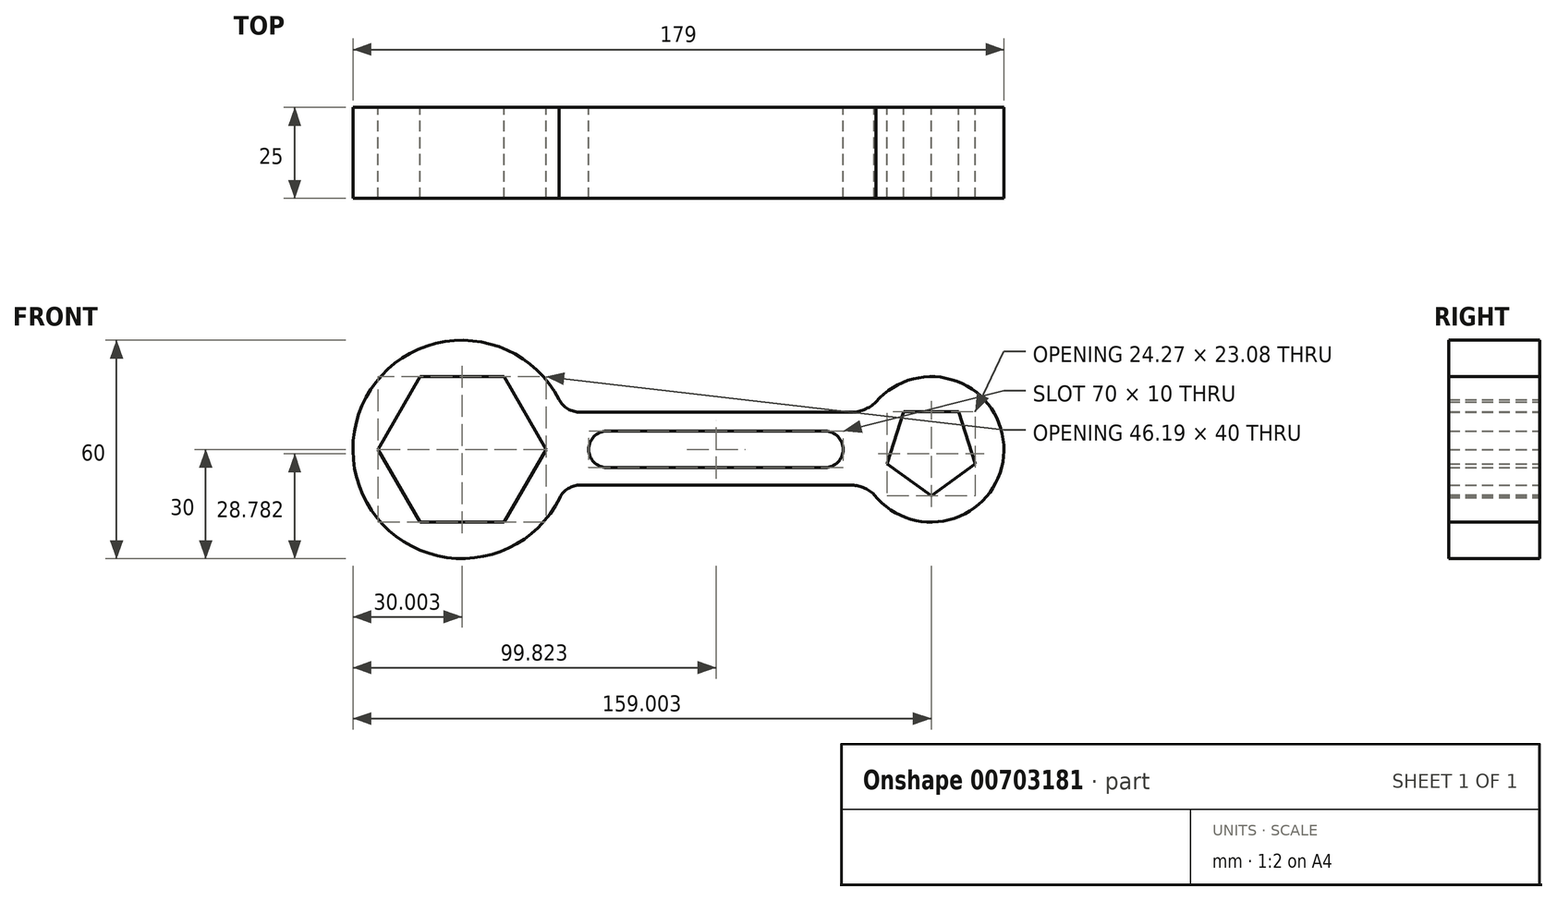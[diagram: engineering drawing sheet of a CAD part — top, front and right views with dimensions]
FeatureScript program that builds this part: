
annotation { "Feature Type Name" : "Feature", "Feature Type Description" : "" }
export const myFeature = defineFeature(function(context is Context, id is Id, definition is map)
    precondition{}
    {
        {
            var Q0;
            Q0=qCreatedBy(makeId("Front.planeOp"),FACE);
            var sketch = newSketch(context, id + "F0", { "sketchPlane" : qUnion([Q0])});
            skArc(sketch, "E0", {"start": v(7.25, 5) * mm, "mid": v(2.25, 0) * mm, "end": v(7.25, -5) * mm});
            skArc(sketch, "E1", {"start": v(67.25, -5) * mm, "mid": v(72.25, 0) * mm, "end": v(67.25, 5) * mm});
            skLineSegment(sketch, "E2", {"start": v(7.25, 5) * mm, "end": v(67.25, 5) * mm});
            skLineSegment(sketch, "E3", {"start": v(7.25, -5) * mm, "end": v(67.25, -5) * mm});
            skCircle(sketch, "E4", {"center": v(-32.57, 0) * mm, "radius": 30 * mm});
            skCircle(sketch, "E5", {"center": v(96.43, 0) * mm, "radius": 20 * mm});
            skPoint(sketch, "E5.centerSnap0", {"position": v(72.25, 0) * mm});
            skCircle(sketch, "E6.cCircle", {"center": v(-32.57, 0) * mm, "radius": 20 * mm, "construction": true});
            skLineSegment(sketch, "E6.0", {"start": v(-44.11, 20) * mm, "end": v(-21.02, 20) * mm});
            skLineSegment(sketch, "E6.1", {"start": v(-21.02, 20) * mm, "end": v(-9.47, 0) * mm});
            skLineSegment(sketch, "E6.2", {"start": v(-9.47, 0) * mm, "end": v(-21.02, -20) * mm});
            skLineSegment(sketch, "E6.3", {"start": v(-21.02, -20) * mm, "end": v(-44.11, -20) * mm});
            skLineSegment(sketch, "E6.4", {"start": v(-44.11, -20) * mm, "end": v(-55.66, 0) * mm});
            skLineSegment(sketch, "E6.5", {"start": v(-55.66, 0) * mm, "end": v(-44.11, 20) * mm});
            skPoint(sketch, "E6.0.midPoint", {"position": v(-32.57, 20) * mm});
            skCircle(sketch, "E7.cCircle", {"center": v(96.43, 0) * mm, "radius": 10.32 * mm, "construction": true});
            skLineSegment(sketch, "E7.0", {"start": v(88.93, 10.32) * mm, "end": v(103.93, 10.32) * mm});
            skLineSegment(sketch, "E7.1", {"start": v(103.93, 10.32) * mm, "end": v(108.57, -3.94) * mm});
            skLineSegment(sketch, "E7.2", {"start": v(108.57, -3.94) * mm, "end": v(96.43, -12.76) * mm});
            skLineSegment(sketch, "E7.3", {"start": v(96.43, -12.76) * mm, "end": v(84.3, -3.94) * mm});
            skLineSegment(sketch, "E7.4", {"start": v(84.3, -3.94) * mm, "end": v(88.93, 10.32) * mm});
            skPoint(sketch, "E7.0.midPoint", {"position": v(96.43, 10.32) * mm});
            skLineSegment(sketch, "E8", {"start": v(0, 10.2) * mm, "end": v(74.24, 10.2) * mm});
            skLineSegment(sketch, "E9", {"start": v(74.24, -9.8) * mm, "end": v(0, -9.8) * mm});
            skArc(sketch, "E10", {"start": v(74.24, 10.2) * mm, "mid": v(78.01, 10.92) * mm, "end": v(81.24, 13) * mm});
            skArc(sketch, "E11", {"start": v(80.77, -12.44) * mm, "mid": v(77.76, -10.5) * mm, "end": v(74.24, -9.8) * mm});
            skArc(sketch, "E12", {"start": v(-5.98, 13.9) * mm, "mid": v(-3.52, 11.2) * mm, "end": v(0, 10.2) * mm});
            skArc(sketch, "E13", {"start": v(0, -9.8) * mm, "mid": v(-3.38, -10.78) * mm, "end": v(-5.73, -13.4) * mm});
            skSolve(sketch);
        }
        {
            var Q0;
            Q0 = qSketchRegion(id + "F0", true);
            extrude(context, id + "F1", {"entities" : qUnion([Q0]), "depth" : 25 * mm, "offsetDistance" : 25 * mm});
        }
    });
